# Revit family: Velios LED - Ceiling based
name_source: partatom
category: Lighting Fixtures
revit_build: Autodesk Revit Architecture 2014 (Build: 20140709_2115(x64)
units: mm (PartAtom-declared; Revit-internal decimal feet)

## types (4) — shared parameters
Apparent Load = 240 VA
ArticleNumber = See URL hyperlink
AssetType = Moveable/Fixed
BSAB 96 = SNB.2
BallastsCELMAEnergyEfficiencyIndex = Class A1/A2
CCSClassCode = UAC
CCSClassName = Belysningsarmatur
CCSTopnode = L
Cassette = Riegens_Steel_Powder coated white RAL901025
Clearance Zones = Yes
Clearance Zones Offset = 60 mm
Color = White
Color Filter = 16777215
ControlGearPosition = Integrated
Description = 70-80-35 General Lighting Systems
Dimming Lamp Color Temperature Shift = <None>
DocumentReference = See URL hyperlink
Documentation = See URL hyperlink
Finish = Powder coated
Frame = Riegens_Steel_Powder coated white RAL901025
Frame Thickness = 10 mm
Glass = Riegens_Glass_opal
HasProtectiveEarth = TRUE
Height 1 = 60 mm
IP_Code = IP20
IfcExportAs = 'IfcLightFixtureType'
IfcExportType = 'NOTDEFINED'
InsulationStandardClass = Class 1
InternalFuse = Only required in emergency versions
LampColourRenderingIndex = Ra>80
LampType = LED
LightFixtureMountingType = Recessed
LightFixturePlacingType = Ceiling
LightSource = LED 4000K
LuminairePowerFactor = >0,9
LuminaireType = Recessed Direct LED Luminaire
Manufacturer = Riegens A/S
ManufacturerURL = www.riegens.com
Material = Steel and Acrylic (PMMA)
NominalVoltage = 220-240V
Optic = Micro-prism lens
PhaseReference = IEC recommendations
PhotometricPerformance = In accordance with BS EN 13032-1
ProductInformation = http://riegens.com
Tilt Angle = 90.00°
Uniclass 1.4 = JY73
Uniclass2 = Pr_70_70_49_43 Light-Emitting Diode (LED) Luminaires
Version = v.1.0

## per-type parameters (varying)
| type | BIMObjectName | Cassette Depth | Cassette Width | Frame Depth | Frame Width | Glass Width | LampRating | Model | ModelReference | Photometric Web File | Shape | Size | TotalWattage |
| Velios LED 300x300 T/L | Velios LED 300x300 T/L.rfa | 284 mm | 270 mm | 295 mm | 295 mm | 70 mm | 13W | Velios LED 300x300 T/L | Velios LED 300x300 T/L | Velios LED 300x300 TL 13W 4000K LensC.ies | Square | 300 x 300 mm | Max. 15W |
| Velios LED 1200x300 T/L | Velios LED 1200x300 T/L.rfa | 1167 mm | 270 mm | 1195 mm | 295 mm | 70 mm | 45W / 47W | Velios LED 1200x300 T/L | Velios LED 1200x300 T/L | Velios LED 300x1200 TL 45W 4000K LensC.ies | Rectangle | 1200 x 300 mm | Max. 50W |
| Velios LED 600x600 T/L | Velios LED 600x600 T/L.rfa | 567 mm | 570 mm | 595 mm | 595 mm | 140 mm | 34W / 35W / 45W | Velios LED 600x600 T/L | Velios LED 600x600 T/L | Velios LED 600x600 TL 45W 4000K LensC.ies | Square | 600 x 600 mm | Max. 38W / 50W |
| Velios LED 1250x312,5 | Velios LED 1250x312,5 T/L.rfa | 1167 mm | 270 mm | 1245 mm | 307 mm | 70 mm | 47W | Velios LED 1250x312,5 T/L | Velios LED 1250x312,5 T/L | Velios LED 300x1200 TL 45W 4000K LensC.ies | Rectangle | 1250 x 312,5 mm | Max. 50W |

## geometry (parser evidence)
native form markers: Sweep x1
no freeform markers — native parametric forms only
